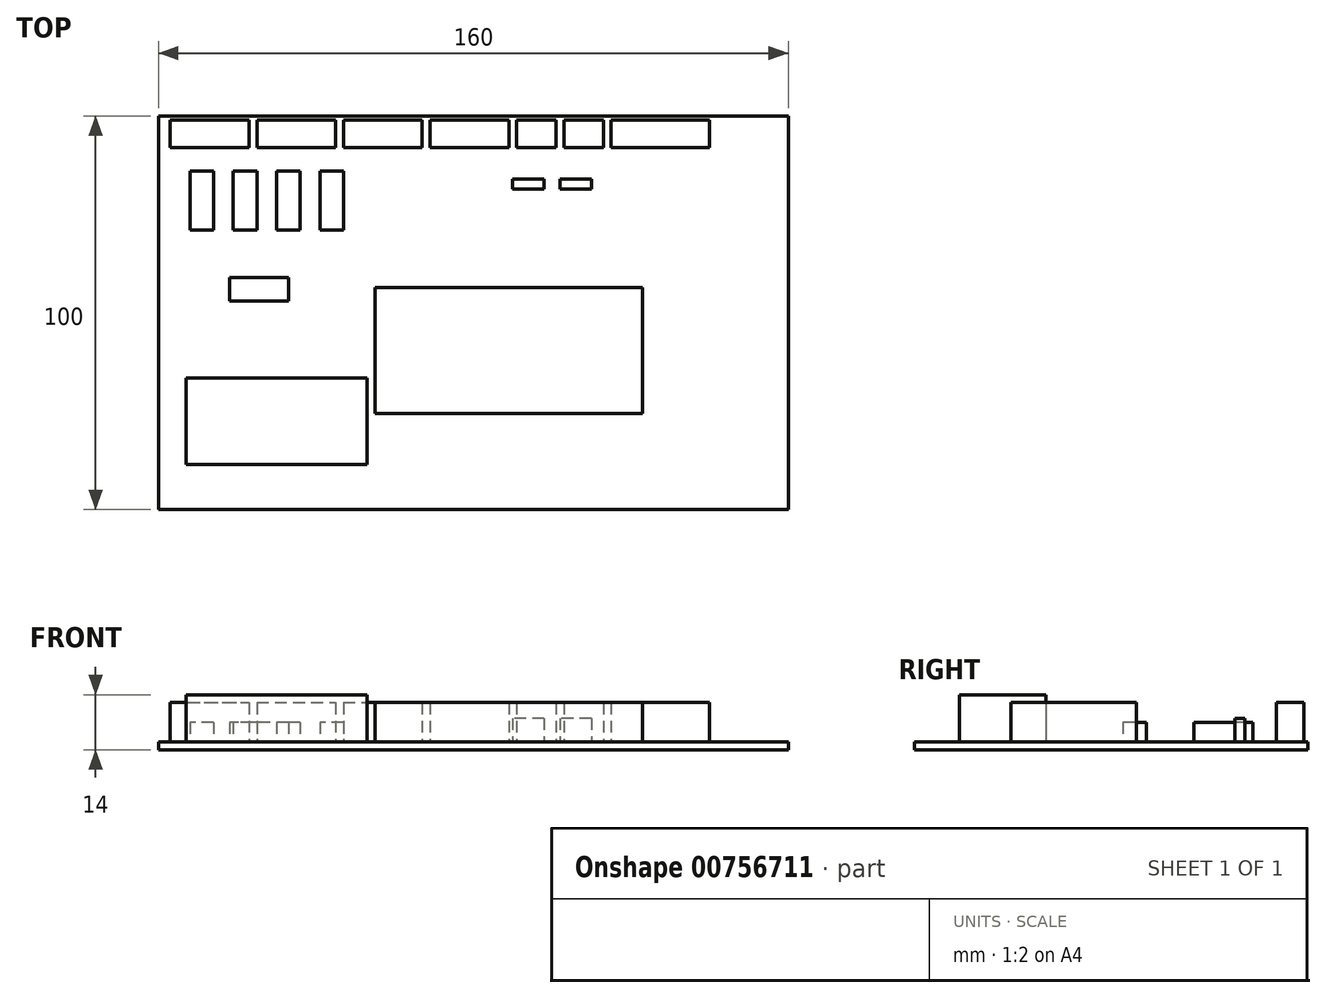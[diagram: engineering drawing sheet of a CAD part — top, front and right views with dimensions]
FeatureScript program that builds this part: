
annotation { "Feature Type Name" : "Feature", "Feature Type Description" : "" }
export const myFeature = defineFeature(function(context is Context, id is Id, definition is map)
    precondition{}
    {
        {
            var Q0;
            Q0=qCreatedBy(makeId("Top.planeOp"),FACE);
            var sketch = newSketch(context, id + "F0", { "sketchPlane" : qUnion([Q0])});
            skLineSegment(sketch, "E0.bottom", {"start": v(80, -50) * mm, "end": v(-80, -50) * mm});
            skLineSegment(sketch, "E0.top", {"start": v(80, 50) * mm, "end": v(-80, 50) * mm});
            skLineSegment(sketch, "E0.left", {"start": v(80, -50) * mm, "end": v(80, 50) * mm});
            skLineSegment(sketch, "E0.right", {"start": v(-80, -50) * mm, "end": v(-80, 50) * mm});
            skPoint(sketch, "E0.middle", {"position": v(0, 0) * mm});
            skSolve(sketch);
        }
        {
            var Q0;
            Q0=makeQuery(id+"F0.imprint","IMPRINT",FACE,{"disambiguationData":[TD([[makeQuery(id+"F0.imprint","IMPRINT",EDGE,{"derivedFrom":sQuery(id+"F0.wireOp",EDGE,"E0.bottom")}),-1.0]])]});
            extrude(context, id + "F1", {"entities" : qUnion([Q0]), "depth" : 2 * mm, "offsetDistance" : 25 * mm});
        }
        {
            var Q0;
            Q0=makeQuery(id+"F1.opExtrude","CAP_FACE",FACE,{"disambiguationData":[OSD([sQuery(id+"F0.wireOp",EDGE,"E0.bottom"),sQuery(id+"F0.wireOp",EDGE,"E0.top"),sQuery(id+"F0.wireOp",EDGE,"E0.left"),sQuery(id+"F0.wireOp",EDGE,"E0.right")])],"isStart":false});
            var sketch = newSketch(context, id + "F2", { "sketchPlane" : qUnion([Q0])});
            skLineSegment(sketch, "E1.bottom", {"start": v(-77, 49) * mm, "end": v(-57, 49) * mm});
            skLineSegment(sketch, "E1.top", {"start": v(-77, 42) * mm, "end": v(-57, 42) * mm});
            skLineSegment(sketch, "E1.left", {"start": v(-77, 49) * mm, "end": v(-77, 42) * mm});
            skLineSegment(sketch, "E1.right", {"start": v(-57, 49) * mm, "end": v(-57, 42) * mm});
            skLineSegment(sketch, "E2.bottom", {"start": v(-55, 49) * mm, "end": v(-35, 49) * mm});
            skLineSegment(sketch, "E2.top", {"start": v(-55, 42) * mm, "end": v(-35, 42) * mm});
            skLineSegment(sketch, "E2.left", {"start": v(-55, 49) * mm, "end": v(-55, 42) * mm});
            skLineSegment(sketch, "E2.right", {"start": v(-35, 49) * mm, "end": v(-35, 42) * mm});
            skLineSegment(sketch, "E3.bottom", {"start": v(-33, 49) * mm, "end": v(-13, 49) * mm});
            skLineSegment(sketch, "E3.top", {"start": v(-33, 42) * mm, "end": v(-13, 42) * mm});
            skLineSegment(sketch, "E3.left", {"start": v(-33, 49) * mm, "end": v(-33, 42) * mm});
            skLineSegment(sketch, "E3.right", {"start": v(-13, 49) * mm, "end": v(-13, 42) * mm});
            skLineSegment(sketch, "E4.bottom", {"start": v(-11, 49) * mm, "end": v(9, 49) * mm});
            skLineSegment(sketch, "E4.top", {"start": v(-11, 42) * mm, "end": v(9, 42) * mm});
            skLineSegment(sketch, "E4.left", {"start": v(-11, 49) * mm, "end": v(-11, 42) * mm});
            skLineSegment(sketch, "E4.right", {"start": v(9, 49) * mm, "end": v(9, 42) * mm});
            skLineSegment(sketch, "E5.bottom", {"start": v(11, 49) * mm, "end": v(21, 49) * mm});
            skLineSegment(sketch, "E5.top", {"start": v(11, 42) * mm, "end": v(21, 42) * mm});
            skLineSegment(sketch, "E5.left", {"start": v(11, 49) * mm, "end": v(11, 42) * mm});
            skLineSegment(sketch, "E5.right", {"start": v(21, 49) * mm, "end": v(21, 42) * mm});
            skLineSegment(sketch, "E6.bottom", {"start": v(23, 49) * mm, "end": v(33, 49) * mm});
            skLineSegment(sketch, "E6.top", {"start": v(23, 42) * mm, "end": v(33, 42) * mm});
            skLineSegment(sketch, "E6.left", {"start": v(23, 49) * mm, "end": v(23, 42) * mm});
            skLineSegment(sketch, "E6.right", {"start": v(33, 49) * mm, "end": v(33, 42) * mm});
            skLineSegment(sketch, "E7.bottom", {"start": v(35, 49) * mm, "end": v(60, 49) * mm});
            skLineSegment(sketch, "E7.top", {"start": v(35, 42) * mm, "end": v(60, 42) * mm});
            skLineSegment(sketch, "E7.left", {"start": v(35, 49) * mm, "end": v(35, 42) * mm});
            skLineSegment(sketch, "E7.right", {"start": v(60, 49) * mm, "end": v(60, 42) * mm});
            skLineSegment(sketch, "E8", {"start": v(-57, 42) * mm, "end": v(-55, 42) * mm, "construction": true});
            skLineSegment(sketch, "E9", {"start": v(-35, 42) * mm, "end": v(-33, 42) * mm, "construction": true});
            skLineSegment(sketch, "E10", {"start": v(-13, 42) * mm, "end": v(-11, 42) * mm, "construction": true});
            skLineSegment(sketch, "E11", {"start": v(9, 42) * mm, "end": v(11, 42) * mm, "construction": true});
            skLineSegment(sketch, "E12", {"start": v(21, 42) * mm, "end": v(23, 42) * mm, "construction": true});
            skLineSegment(sketch, "E13", {"start": v(33, 42) * mm, "end": v(35, 42) * mm, "construction": true});
            skSolve(sketch);
        }
        {
            var Q0;
            Q0=makeQuery(id+"F2.imprint","IMPRINT",FACE,{"disambiguationData":[TD([[makeQuery(id+"F2.imprint","IMPRINT",EDGE,{"derivedFrom":sQuery(id+"F2.wireOp",EDGE,"E1.bottom")}),-1.0]])]});
            var Q1;
            Q1=makeQuery(id+"F2.imprint","IMPRINT",FACE,{"disambiguationData":[TD([[makeQuery(id+"F2.imprint","IMPRINT",EDGE,{"derivedFrom":sQuery(id+"F2.wireOp",EDGE,"E2.bottom")}),-1.0]])]});
            var Q2;
            Q2=makeQuery(id+"F2.imprint","IMPRINT",FACE,{"disambiguationData":[TD([[makeQuery(id+"F2.imprint","IMPRINT",EDGE,{"derivedFrom":sQuery(id+"F2.wireOp",EDGE,"E3.bottom")}),-1.0]])]});
            var Q3;
            Q3=makeQuery(id+"F2.imprint","IMPRINT",FACE,{"disambiguationData":[TD([[makeQuery(id+"F2.imprint","IMPRINT",EDGE,{"derivedFrom":sQuery(id+"F2.wireOp",EDGE,"E5.bottom")}),-1.0]])]});
            var Q4;
            Q4=makeQuery(id+"F2.imprint","IMPRINT",FACE,{"disambiguationData":[TD([[makeQuery(id+"F2.imprint","IMPRINT",EDGE,{"derivedFrom":sQuery(id+"F2.wireOp",EDGE,"E4.bottom")}),-1.0]])]});
            var Q5;
            Q5=makeQuery(id+"F2.imprint","IMPRINT",FACE,{"disambiguationData":[TD([[makeQuery(id+"F2.imprint","IMPRINT",EDGE,{"derivedFrom":sQuery(id+"F2.wireOp",EDGE,"E6.bottom")}),-1.0]])]});
            var Q6;
            Q6=makeQuery(id+"F2.imprint","IMPRINT",FACE,{"disambiguationData":[TD([[makeQuery(id+"F2.imprint","IMPRINT",EDGE,{"derivedFrom":sQuery(id+"F2.wireOp",EDGE,"E7.bottom")}),-1.0]])]});
            extrude(context, id + "F3", {"entities" : qUnion([Q0, Q1, Q2, Q3, Q4, Q5, Q6]), "depth" : 10 * mm, "offsetDistance" : 25 * mm});
        }
        {
            var Q0;
            Q0=makeQuery(id+"F1.opExtrude","CAP_FACE",FACE,{"disambiguationData":[OSD([sQuery(id+"F0.wireOp",EDGE,"E0.bottom"),sQuery(id+"F0.wireOp",EDGE,"E0.top"),sQuery(id+"F0.wireOp",EDGE,"E0.left"),sQuery(id+"F0.wireOp",EDGE,"E0.right")])],"isStart":false});
            var sketch = newSketch(context, id + "F4", { "sketchPlane" : qUnion([Q0])});
            skLineSegment(sketch, "E14.bottom", {"start": v(-66, 36) * mm, "end": v(-72, 36) * mm});
            skLineSegment(sketch, "E14.top", {"start": v(-66, 21) * mm, "end": v(-72, 21) * mm});
            skLineSegment(sketch, "E14.left", {"start": v(-66, 36) * mm, "end": v(-66, 21) * mm});
            skLineSegment(sketch, "E14.right", {"start": v(-72, 36) * mm, "end": v(-72, 21) * mm});
            skLineSegment(sketch, "E15.bottom", {"start": v(-55, 36) * mm, "end": v(-61, 36) * mm});
            skLineSegment(sketch, "E15.top", {"start": v(-55, 21) * mm, "end": v(-61, 21) * mm});
            skLineSegment(sketch, "E15.left", {"start": v(-55, 36) * mm, "end": v(-55, 21) * mm});
            skLineSegment(sketch, "E15.right", {"start": v(-61, 36) * mm, "end": v(-61, 21) * mm});
            skLineSegment(sketch, "E16.bottom", {"start": v(-44, 36) * mm, "end": v(-50, 36) * mm});
            skLineSegment(sketch, "E16.top", {"start": v(-44, 21) * mm, "end": v(-50, 21) * mm});
            skLineSegment(sketch, "E16.left", {"start": v(-44, 36) * mm, "end": v(-44, 21) * mm});
            skLineSegment(sketch, "E16.right", {"start": v(-50, 36) * mm, "end": v(-50, 21) * mm});
            skLineSegment(sketch, "E17.bottom", {"start": v(-33, 36) * mm, "end": v(-39, 36) * mm});
            skLineSegment(sketch, "E17.top", {"start": v(-33, 21) * mm, "end": v(-39, 21) * mm});
            skLineSegment(sketch, "E17.left", {"start": v(-33, 36) * mm, "end": v(-33, 21) * mm});
            skLineSegment(sketch, "E17.right", {"start": v(-39, 36) * mm, "end": v(-39, 21) * mm});
            skLineSegment(sketch, "E18.bottom", {"start": v(-47, 9) * mm, "end": v(-62, 9) * mm});
            skLineSegment(sketch, "E18.top", {"start": v(-47, 3) * mm, "end": v(-62, 3) * mm});
            skLineSegment(sketch, "E18.left", {"start": v(-47, 9) * mm, "end": v(-47, 3) * mm});
            skLineSegment(sketch, "E18.right", {"start": v(-62, 9) * mm, "end": v(-62, 3) * mm});
            skLineSegment(sketch, "E19", {"start": v(-66, 36) * mm, "end": v(-61, 36) * mm, "construction": true});
            skLineSegment(sketch, "E20", {"start": v(-55, 36) * mm, "end": v(-50, 36) * mm, "construction": true});
            skLineSegment(sketch, "E21", {"start": v(-44, 36) * mm, "end": v(-39, 36) * mm, "construction": true});
            skLineSegment(sketch, "E22", {"start": v(-47, 21) * mm, "end": v(-47, 9) * mm, "construction": true});
            skSolve(sketch);
        }
        {
            var Q0;
            Q0 = qSketchRegion(id + "F4", true);
            extrude(context, id + "F5", {"entities" : qUnion([Q0]), "depth" : 5 * mm, "offsetDistance" : 25 * mm});
        }
        {
            var Q0;
            Q0=makeQuery(id+"F1.opExtrude","CAP_FACE",FACE,{"disambiguationData":[OSD([sQuery(id+"F0.wireOp",EDGE,"E0.bottom"),sQuery(id+"F0.wireOp",EDGE,"E0.top"),sQuery(id+"F0.wireOp",EDGE,"E0.left"),sQuery(id+"F0.wireOp",EDGE,"E0.right")])],"isStart":false});
            var sketch = newSketch(context, id + "F6", { "sketchPlane" : qUnion([Q0])});
            skLineSegment(sketch, "E23.bottom", {"start": v(18, 34) * mm, "end": v(10, 34) * mm});
            skLineSegment(sketch, "E23.top", {"start": v(18, 31.5) * mm, "end": v(10, 31.5) * mm});
            skLineSegment(sketch, "E23.left", {"start": v(18, 34) * mm, "end": v(18, 31.5) * mm});
            skLineSegment(sketch, "E23.right", {"start": v(10, 34) * mm, "end": v(10, 31.5) * mm});
            skLineSegment(sketch, "E24.bottom", {"start": v(30, 34) * mm, "end": v(22, 34) * mm});
            skLineSegment(sketch, "E24.top", {"start": v(30, 31.5) * mm, "end": v(22, 31.5) * mm});
            skLineSegment(sketch, "E24.left", {"start": v(30, 34) * mm, "end": v(30, 31.5) * mm});
            skLineSegment(sketch, "E24.right", {"start": v(22, 34) * mm, "end": v(22, 31.5) * mm});
            skSolve(sketch);
        }
        {
            var Q0;
            Q0 = qSketchRegion(id + "F6", true);
            extrude(context, id + "F7", {"entities" : qUnion([Q0]), "depth" : 6 * mm, "offsetDistance" : 25 * mm});
        }
        {
            var Q0;
            Q0=makeQuery(id+"F1.opExtrude","CAP_FACE",FACE,{"disambiguationData":[OSD([sQuery(id+"F0.wireOp",EDGE,"E0.bottom"),sQuery(id+"F0.wireOp",EDGE,"E0.top"),sQuery(id+"F0.wireOp",EDGE,"E0.left"),sQuery(id+"F0.wireOp",EDGE,"E0.right")])],"isStart":false});
            var sketch = newSketch(context, id + "F8", { "sketchPlane" : qUnion([Q0])});
            skLineSegment(sketch, "E25.bottom", {"start": v(43, 6.5) * mm, "end": v(-25, 6.5) * mm});
            skLineSegment(sketch, "E25.top", {"start": v(43, -25.5) * mm, "end": v(-25, -25.5) * mm});
            skLineSegment(sketch, "E25.left", {"start": v(43, 6.5) * mm, "end": v(43, -25.5) * mm});
            skLineSegment(sketch, "E25.right", {"start": v(-25, 6.5) * mm, "end": v(-25, -25.5) * mm});
            skSolve(sketch);
        }
        {
            var Q0;
            Q0 = qSketchRegion(id + "F8", true);
            extrude(context, id + "F9", {"entities" : qUnion([Q0]), "depth" : 10 * mm, "offsetDistance" : 25 * mm});
        }
        {
            var Q0;
            Q0=makeQuery(id+"F1.opExtrude","CAP_FACE",FACE,{"disambiguationData":[OSD([sQuery(id+"F0.wireOp",EDGE,"E0.bottom"),sQuery(id+"F0.wireOp",EDGE,"E0.top"),sQuery(id+"F0.wireOp",EDGE,"E0.left"),sQuery(id+"F0.wireOp",EDGE,"E0.right")])],"isStart":false});
            var sketch = newSketch(context, id + "F10", { "sketchPlane" : qUnion([Q0])});
            skLineSegment(sketch, "E26.bottom", {"start": v(-27, -16.5) * mm, "end": v(-73, -16.5) * mm});
            skLineSegment(sketch, "E26.top", {"start": v(-27, -38.5) * mm, "end": v(-73, -38.5) * mm});
            skLineSegment(sketch, "E26.left", {"start": v(-27, -16.5) * mm, "end": v(-27, -38.5) * mm});
            skLineSegment(sketch, "E26.right", {"start": v(-73, -16.5) * mm, "end": v(-73, -38.5) * mm});
            skSolve(sketch);
        }
        {
            var Q0;
            Q0 = qSketchRegion(id + "F10", true);
            extrude(context, id + "F11", {"entities" : qUnion([Q0]), "depth" : 12 * mm, "offsetDistance" : 25 * mm});
        }
    });
